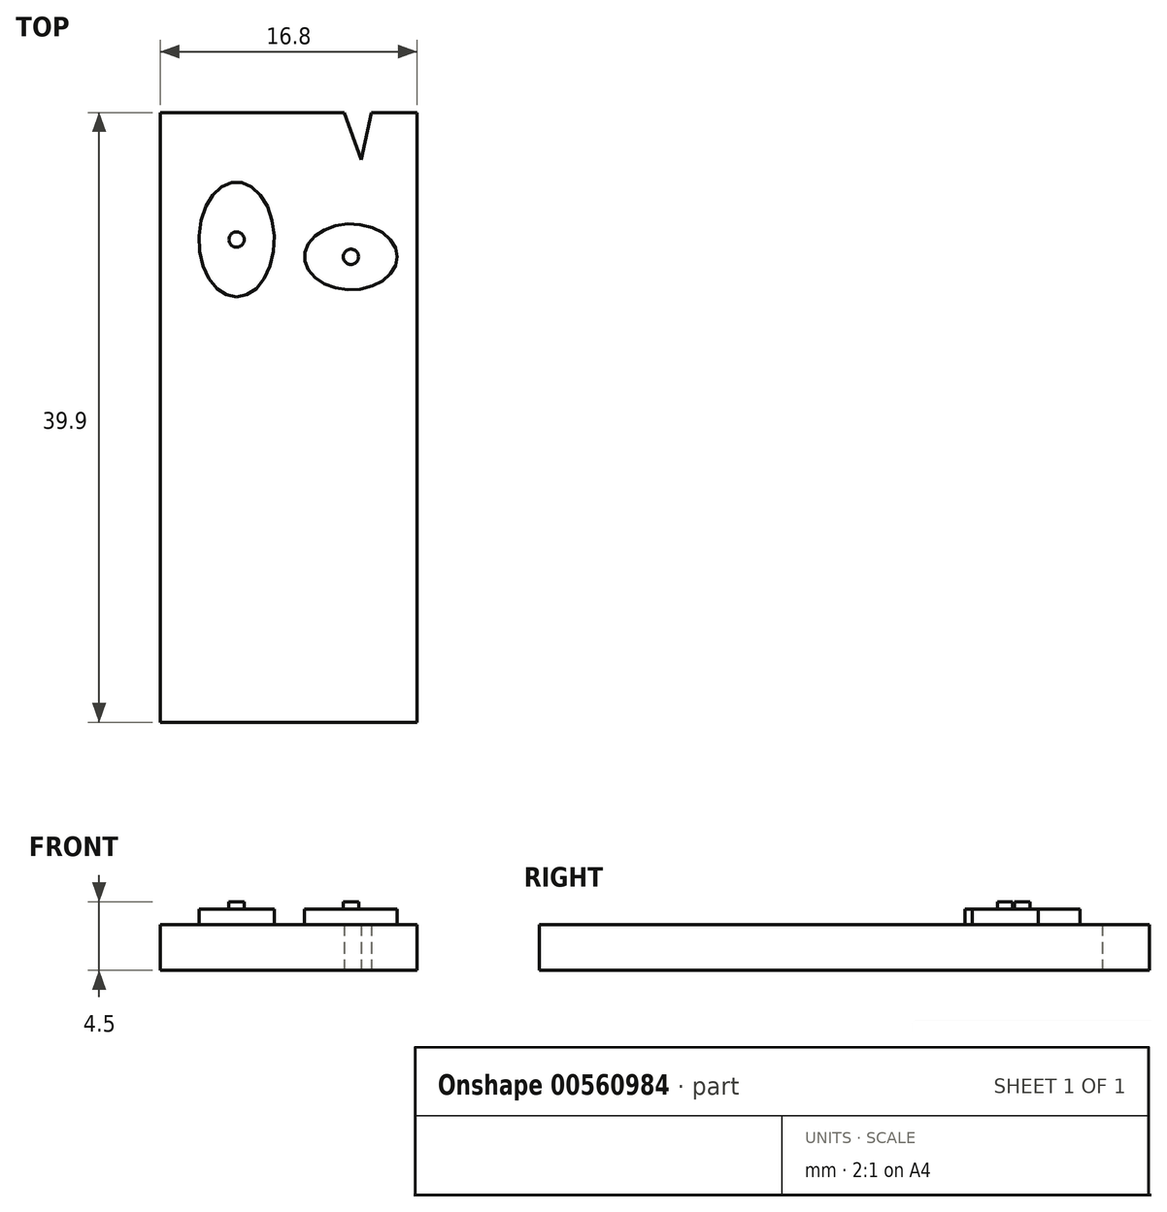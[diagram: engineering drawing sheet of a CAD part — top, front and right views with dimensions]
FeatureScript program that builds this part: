
annotation { "Feature Type Name" : "Feature", "Feature Type Description" : "" }
export const myFeature = defineFeature(function(context is Context, id is Id, definition is map)
    precondition{}
    {
        {
            var Q0;
            Q0=qCreatedBy(makeId("Top.planeOp"),FACE);
            var sketch = newSketch(context, id + "F0", { "sketchPlane" : qUnion([Q0])});
            skLineSegment(sketch, "E0", {"start": v(-54.25, 54.86) * mm, "end": v(-42.23, 54.86) * mm});
            skLineSegment(sketch, "E1", {"start": v(-42.23, 54.86) * mm, "end": v(-41.11, 51.77) * mm});
            skLineSegment(sketch, "E2", {"start": v(-41.11, 51.77) * mm, "end": v(-40.43, 54.86) * mm});
            skLineSegment(sketch, "E3", {"start": v(-40.43, 54.86) * mm, "end": v(-37.45, 54.86) * mm});
            skLineSegment(sketch, "E4", {"start": v(-37.45, 54.86) * mm, "end": v(-37.45, 14.96) * mm});
            skLineSegment(sketch, "E5", {"start": v(-37.45, 14.96) * mm, "end": v(-54.25, 14.96) * mm});
            skLineSegment(sketch, "E6", {"start": v(-54.25, 14.96) * mm, "end": v(-54.25, 54.86) * mm});
            skEllipse(sketch, "E7", {"center": v(-49.26, 46.55) * mm, "majorRadius": 3.76 * mm, "minorRadius": 2.47 * mm, "majorAxis": v(0, -1)});
            skEllipse(sketch, "E8", {"center": v(-41.78, 45.42) * mm, "majorRadius": 3.03 * mm, "minorRadius": 2.16 * mm, "majorAxis": v(1, 0)});
            skArc(sketch, "E9", {"start": v(-49.55, 37.43) * mm, "mid": v(-45.5, 36.03) * mm, "end": v(-41.4, 37.28) * mm});
            skCircle(sketch, "E10", {"center": v(-49.26, 46.55) * mm, "radius": 0.5 * mm});
            skCircle(sketch, "E11", {"center": v(-41.78, 45.42) * mm, "radius": 0.5 * mm});
            skSolve(sketch);
        }
        {
            var Q0;
            Q0 = qSketchRegion(id + "F0", true);
            extrude(context, id + "F1", {"entities" : qUnion([Q0]), "depth" : 3 * mm, "offsetDistance" : 25 * mm});
        }
        {
            var Q0;
            Q0=makeQuery(id+"F0.imprint","IMPRINT",FACE,{"disambiguationData":[TD([[makeQuery(id+"F0.imprint","IMPRINT",EDGE,{"derivedFrom":sQuery(id+"F0.wireOp",EDGE,"E7")}),1.0]])]});
            var Q1;
            Q1=makeQuery(id+"F0.imprint","IMPRINT",FACE,{"disambiguationData":[TD([[makeQuery(id+"F0.imprint","IMPRINT",EDGE,{"derivedFrom":sQuery(id+"F0.wireOp",EDGE,"E8")}),1.0]])]});
            extrude(context, id + "F2", {"entities" : qUnion([Q0, Q1]), "operationType" : NewBodyOperationType.ADD, "depth" : 4 * mm, "offsetDistance" : 25 * mm});
        }
        {
            var Q0;
            Q0=makeQuery(id+"F0.imprint","IMPRINT",FACE,{"disambiguationData":[TD([[makeQuery(id+"F0.imprint","IMPRINT",EDGE,{"derivedFrom":sQuery(id+"F0.wireOp",EDGE,"E10")}),1.0]])]});
            var Q1;
            Q1=makeQuery(id+"F0.imprint","IMPRINT",FACE,{"disambiguationData":[TD([[makeQuery(id+"F0.imprint","IMPRINT",EDGE,{"derivedFrom":sQuery(id+"F0.wireOp",EDGE,"E11")}),1.0]])]});
            extrude(context, id + "F3", {"entities" : qUnion([Q0, Q1]), "operationType" : NewBodyOperationType.ADD, "depth" : 4.5 * mm, "offsetDistance" : 25 * mm});
        }
    });
